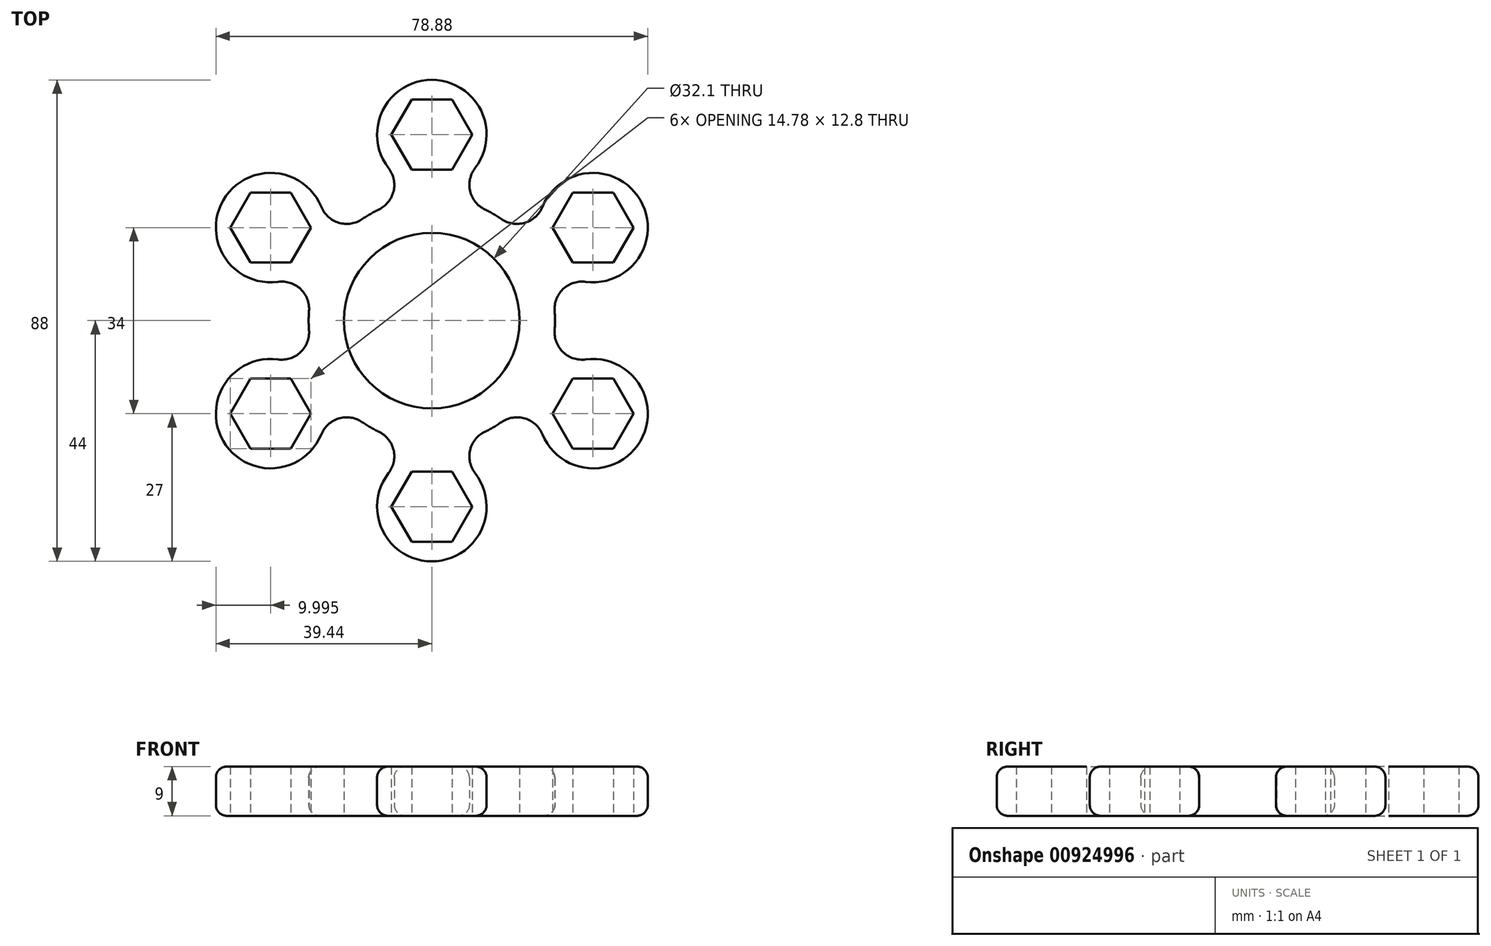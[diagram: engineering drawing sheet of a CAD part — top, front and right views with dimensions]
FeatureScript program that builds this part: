
annotation { "Feature Type Name" : "Feature", "Feature Type Description" : "" }
export const myFeature = defineFeature(function(context is Context, id is Id, definition is map)
    precondition{}
    {
        {
            var Q0;
            Q0=qCreatedBy(makeId("Top.planeOp"),FACE);
            var sketch = newSketch(context, id + "F0", { "sketchPlane" : qUnion([Q0])});
            skCircle(sketch, "E0", {"center": v(0, 0) * mm, "radius": 16.05 * mm});
            skCircle(sketch, "E1", {"center": v(0, 0) * mm, "radius": 22.5 * mm});
            skCircle(sketch, "E2", {"center": v(0, 34) * mm, "radius": 10 * mm});
            skCircle(sketch, "E3", {"center": v(29.44, -17) * mm, "radius": 10 * mm});
            skCircle(sketch, "E4", {"center": v(-29.44, 17) * mm, "radius": 10 * mm});
            skLineSegment(sketch, "E5", {"start": v(0, 0) * mm, "end": v(29.44, -17) * mm, "construction": true});
            skLineSegment(sketch, "E6", {"start": v(0, 0) * mm, "end": v(-29.44, 17) * mm, "construction": true});
            skCircle(sketch, "E7.cCircle", {"center": v(0, 34) * mm, "radius": 6.4 * mm, "construction": true});
            skLineSegment(sketch, "E7.0", {"start": v(3.7, 27.6) * mm, "end": v(-3.7, 27.6) * mm});
            skLineSegment(sketch, "E7.1", {"start": v(-3.7, 27.6) * mm, "end": v(-7.4, 34) * mm});
            skLineSegment(sketch, "E7.2", {"start": v(-7.4, 34) * mm, "end": v(-3.7, 40.4) * mm});
            skLineSegment(sketch, "E7.3", {"start": v(-3.7, 40.4) * mm, "end": v(3.7, 40.4) * mm});
            skLineSegment(sketch, "E7.4", {"start": v(3.7, 40.4) * mm, "end": v(7.4, 34) * mm});
            skLineSegment(sketch, "E7.5", {"start": v(7.4, 34) * mm, "end": v(3.7, 27.6) * mm});
            skPoint(sketch, "E7.0.midPoint", {"position": v(0, 27.6) * mm});
            skCircle(sketch, "E8.cCircle", {"center": v(29.44, -17) * mm, "radius": 6.4 * mm, "construction": true});
            skLineSegment(sketch, "E8.0", {"start": v(25.75, -10.6) * mm, "end": v(33.14, -10.6) * mm});
            skLineSegment(sketch, "E8.1", {"start": v(33.14, -10.6) * mm, "end": v(36.83, -17) * mm});
            skLineSegment(sketch, "E8.2", {"start": v(36.83, -17) * mm, "end": v(33.14, -23.4) * mm});
            skLineSegment(sketch, "E8.3", {"start": v(33.14, -23.4) * mm, "end": v(25.75, -23.4) * mm});
            skLineSegment(sketch, "E8.4", {"start": v(25.75, -23.4) * mm, "end": v(22.05, -17) * mm});
            skLineSegment(sketch, "E8.5", {"start": v(22.05, -17) * mm, "end": v(25.75, -10.6) * mm});
            skPoint(sketch, "E8.0.midPoint", {"position": v(29.44, -10.6) * mm});
            skCircle(sketch, "E9.cCircle", {"center": v(-29.44, 17) * mm, "radius": 6.4 * mm, "construction": true});
            skLineSegment(sketch, "E9.0", {"start": v(-22.05, 17) * mm, "end": v(-25.75, 10.6) * mm});
            skLineSegment(sketch, "E9.1", {"start": v(-25.75, 10.6) * mm, "end": v(-33.14, 10.6) * mm});
            skLineSegment(sketch, "E9.2", {"start": v(-33.14, 10.6) * mm, "end": v(-36.83, 17) * mm});
            skLineSegment(sketch, "E9.3", {"start": v(-36.83, 17) * mm, "end": v(-33.14, 23.4) * mm});
            skLineSegment(sketch, "E9.4", {"start": v(-33.14, 23.4) * mm, "end": v(-25.75, 23.4) * mm});
            skLineSegment(sketch, "E9.5", {"start": v(-25.75, 23.4) * mm, "end": v(-22.05, 17) * mm});
            skPoint(sketch, "E9.0.midPoint", {"position": v(-23.9, 13.8) * mm});
            skArc(sketch, "E10", {"start": v(-20.19, 20.78) * mm, "mid": v(-17, 17.88) * mm, "end": v(-12.73, 18.55) * mm});
            skArc(sketch, "E11", {"start": v(-22.43, 1.75) * mm, "mid": v(-23.98, 5.77) * mm, "end": v(-28.1, 7.1) * mm});
            skArc(sketch, "E12", {"start": v(-9.7, 20.3) * mm, "mid": v(-7, 23.66) * mm, "end": v(-7.9, 27.88) * mm});
            skArc(sketch, "E13", {"start": v(7.9, 27.88) * mm, "mid": v(7, 23.66) * mm, "end": v(9.7, 20.3) * mm});
            skArc(sketch, "E14", {"start": v(22.43, -1.75) * mm, "mid": v(23.98, -5.77) * mm, "end": v(28.1, -7.1) * mm});
            skArc(sketch, "E15", {"start": v(20.19, -20.78) * mm, "mid": v(17, -17.88) * mm, "end": v(12.73, -18.55) * mm});
            skCircle(sketch, "E16", {"center": v(0, 0) * mm, "radius": 34 * mm, "construction": true});
            skLineSegment(sketch, "E17", {"start": v(0, 0) * mm, "end": v(-29.44, -17) * mm, "construction": true});
            skLineSegment(sketch, "E18", {"start": v(0, 0) * mm, "end": v(0, -34) * mm, "construction": true});
            skLineSegment(sketch, "E19", {"start": v(0, 0) * mm, "end": v(29.44, 17) * mm, "construction": true});
            skCircle(sketch, "E20", {"center": v(-29.44, -17) * mm, "radius": 10 * mm});
            skCircle(sketch, "E21", {"center": v(0, -34) * mm, "radius": 10 * mm});
            skCircle(sketch, "E22", {"center": v(29.44, 17) * mm, "radius": 10 * mm});
            skArc(sketch, "E23", {"start": v(-22.43, -1.75) * mm, "mid": v(-23.98, -5.77) * mm, "end": v(-28.1, -7.1) * mm});
            skArc(sketch, "E24", {"start": v(-12.73, -18.55) * mm, "mid": v(-17, -17.88) * mm, "end": v(-20.19, -20.78) * mm});
            skArc(sketch, "E25", {"start": v(-9.7, -20.3) * mm, "mid": v(-7, -23.66) * mm, "end": v(-7.9, -27.88) * mm});
            skArc(sketch, "E26", {"start": v(9.7, -20.3) * mm, "mid": v(7, -23.66) * mm, "end": v(7.9, -27.88) * mm});
            skArc(sketch, "E27", {"start": v(22.43, 1.75) * mm, "mid": v(23.98, 5.77) * mm, "end": v(28.1, 7.1) * mm});
            skArc(sketch, "E28", {"start": v(12.73, 18.55) * mm, "mid": v(17, 17.88) * mm, "end": v(20.19, 20.78) * mm});
            skCircle(sketch, "E29.cCircle", {"center": v(29.44, 17) * mm, "radius": 6.4 * mm, "construction": true});
            skLineSegment(sketch, "E29.0", {"start": v(33.14, 10.6) * mm, "end": v(25.75, 10.6) * mm});
            skLineSegment(sketch, "E29.1", {"start": v(25.75, 10.6) * mm, "end": v(22.05, 17) * mm});
            skLineSegment(sketch, "E29.2", {"start": v(22.05, 17) * mm, "end": v(25.75, 23.4) * mm});
            skLineSegment(sketch, "E29.3", {"start": v(25.75, 23.4) * mm, "end": v(33.14, 23.4) * mm});
            skLineSegment(sketch, "E29.4", {"start": v(33.14, 23.4) * mm, "end": v(36.83, 17) * mm});
            skLineSegment(sketch, "E29.5", {"start": v(36.83, 17) * mm, "end": v(33.14, 10.6) * mm});
            skPoint(sketch, "E29.0.midPoint", {"position": v(29.44, 10.6) * mm});
            skCircle(sketch, "E30.cCircle", {"center": v(0, -34) * mm, "radius": 6.4 * mm, "construction": true});
            skLineSegment(sketch, "E30.0", {"start": v(-3.7, -27.6) * mm, "end": v(3.7, -27.6) * mm});
            skLineSegment(sketch, "E30.1", {"start": v(3.7, -27.6) * mm, "end": v(7.4, -34) * mm});
            skLineSegment(sketch, "E30.2", {"start": v(7.4, -34) * mm, "end": v(3.7, -40.4) * mm});
            skLineSegment(sketch, "E30.3", {"start": v(3.7, -40.4) * mm, "end": v(-3.7, -40.4) * mm});
            skLineSegment(sketch, "E30.4", {"start": v(-3.7, -40.4) * mm, "end": v(-7.4, -34) * mm});
            skLineSegment(sketch, "E30.5", {"start": v(-7.4, -34) * mm, "end": v(-3.7, -27.6) * mm});
            skPoint(sketch, "E30.0.midPoint", {"position": v(0, -27.6) * mm});
            skCircle(sketch, "E31.cCircle", {"center": v(-29.44, -17) * mm, "radius": 6.4 * mm, "construction": true});
            skLineSegment(sketch, "E31.0", {"start": v(-25.75, -10.6) * mm, "end": v(-22.05, -17) * mm});
            skLineSegment(sketch, "E31.1", {"start": v(-22.05, -17) * mm, "end": v(-25.75, -23.4) * mm});
            skLineSegment(sketch, "E31.2", {"start": v(-25.75, -23.4) * mm, "end": v(-33.14, -23.4) * mm});
            skLineSegment(sketch, "E31.3", {"start": v(-33.14, -23.4) * mm, "end": v(-36.83, -17) * mm});
            skLineSegment(sketch, "E31.4", {"start": v(-36.83, -17) * mm, "end": v(-33.14, -10.6) * mm});
            skLineSegment(sketch, "E31.5", {"start": v(-33.14, -10.6) * mm, "end": v(-25.75, -10.6) * mm});
            skPoint(sketch, "E31.0.midPoint", {"position": v(-23.9, -13.8) * mm});
            skSolve(sketch);
        }
        {
            var Q0;
            Q0 = qSketchRegion(id + "F0", true);
            var Q1;
            {var subQ0=sQuery(id+"F0.wireOp",EDGE,"E4");var subQ1=sQuery(id+"F0.wireOp",EDGE,"E1");var subQ2=makeQuery(id+"F0.imprint","INTERSECT",VERTEX,{"disambiguationData":[OD(0.0)],"derivedFrom":[subQ1,subQ0]});Q1=makeQuery(id+"F0.imprint","IMPRINT",FACE,{"disambiguationData":[TD([[makeQuery(id+"F0.imprint","IMPRINT",EDGE,{"disambiguationData":[TD([[subQ2,-1.0]])],"derivedFrom":subQ1}),1.0]])]});}
            var Q2;
            {var subQ0=sQuery(id+"F0.wireOp",EDGE,"E2");var subQ1=sQuery(id+"F0.wireOp",EDGE,"E1");var subQ2=makeQuery(id+"F0.imprint","INTERSECT",VERTEX,{"disambiguationData":[OD(0.0)],"derivedFrom":[subQ1,subQ0]});Q2=makeQuery(id+"F0.imprint","IMPRINT",FACE,{"disambiguationData":[TD([[makeQuery(id+"F0.imprint","IMPRINT",EDGE,{"disambiguationData":[TD([[subQ2,-1.0]])],"derivedFrom":subQ1}),1.0]])]});}
            var Q3;
            {var subQ0=sQuery(id+"F0.wireOp",EDGE,"E3");var subQ1=sQuery(id+"F0.wireOp",EDGE,"E1");var subQ2=makeQuery(id+"F0.imprint","INTERSECT",VERTEX,{"disambiguationData":[OD(0.0)],"derivedFrom":[subQ1,subQ0]});Q3=makeQuery(id+"F0.imprint","IMPRINT",FACE,{"disambiguationData":[TD([[makeQuery(id+"F0.imprint","IMPRINT",EDGE,{"disambiguationData":[TD([[subQ2,-1.0]])],"derivedFrom":subQ1}),1.0]])]});}
            extrude(context, id + "F1", {"entities" : qUnion([Q0, Q1, Q2, Q3]), "depth" : 9 * mm, "offsetDistance" : 25 * mm});
        }
        {
            var Q0;
            Q0=makeQuery(id+"F1.opExtrude","CAP_EDGE",EDGE,{"disambiguationData":[OSD([sQuery(id+"F0.wireOp",EDGE,"E11")])],"isStart":false});
            var Q1;
            Q1=makeQuery(id+"F1.opExtrude","CAP_EDGE",EDGE,{"disambiguationData":[OSD([sQuery(id+"F0.wireOp",EDGE,"E11")])],"isStart":true});
            fillet(context, id + "F2", {"entities" : qUnion([Q0, Q1]), "radius" : 2 * mm, "tangentPropagation" : true, "allowEdgeOverflow" : false});
        }
    });
